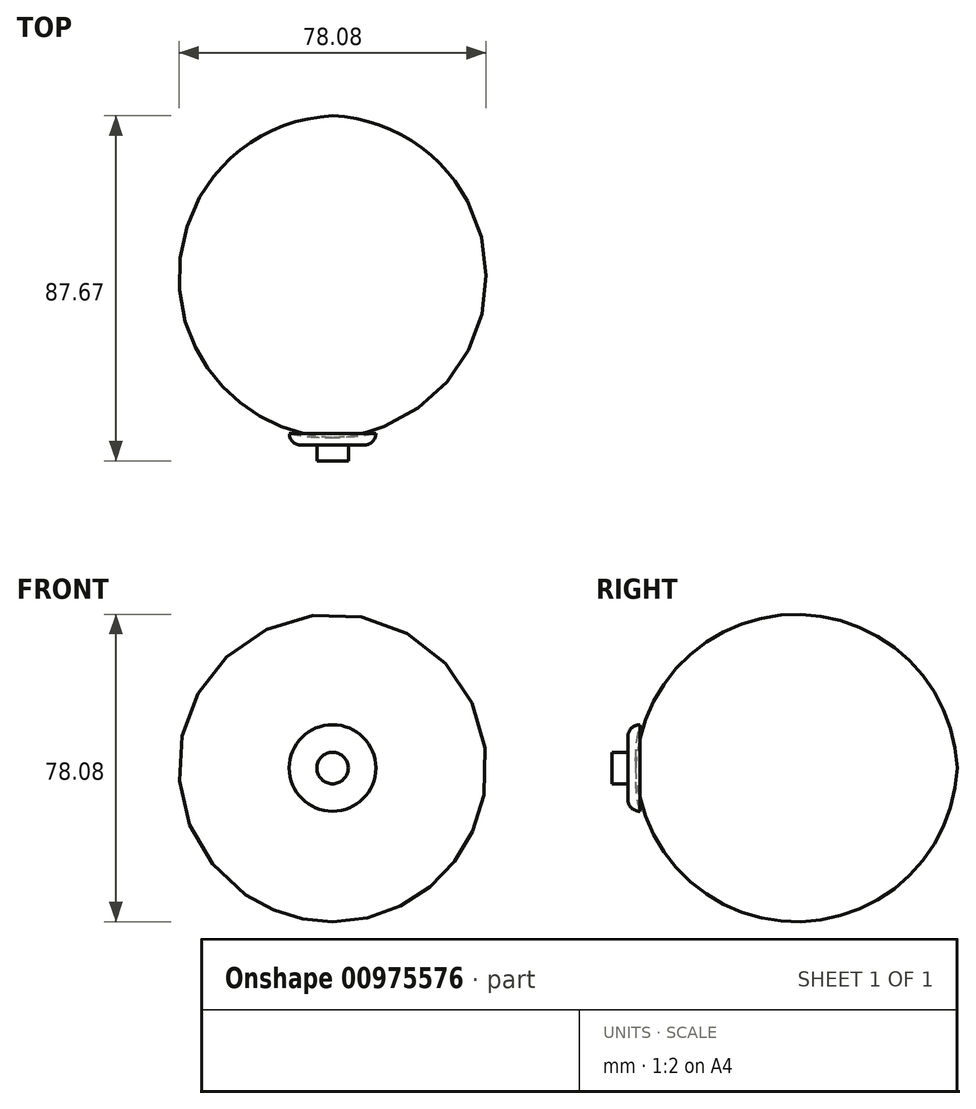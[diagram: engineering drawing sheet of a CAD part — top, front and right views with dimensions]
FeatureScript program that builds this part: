
annotation { "Feature Type Name" : "Feature", "Feature Type Description" : "" }
export const myFeature = defineFeature(function(context is Context, id is Id, definition is map)
    precondition{}
    {
        {
            var Q0;
            Q0=qCreatedBy(makeId("Top.planeOp"),FACE);
            var sketch = newSketch(context, id + "F0", { "sketchPlane" : qUnion([Q0])});
            skLineSegment(sketch, "E0", {"start": v(0, 0) * mm, "end": v(0, -2) * mm});
            skLineSegment(sketch, "E1", {"start": v(0, -2) * mm, "end": v(11, -2) * mm});
            skLineSegment(sketch, "E2", {"start": v(11, -2) * mm, "end": v(11, 1) * mm});
            skArc(sketch, "E3", {"start": v(0, 0) * mm, "mid": v(5.53, 0.13) * mm, "end": v(11, 1) * mm});
            skSolve(sketch);
        }
        {
            var Q0;
            Q0=makeQuery(id+"F0.imprint","IMPRINT",FACE,{"disambiguationData":[TD([[makeQuery(id+"F0.imprint","IMPRINT",EDGE,{"derivedFrom":sQuery(id+"F0.wireOp",EDGE,"E0")}),1.0]])]});
            var Q1;
            Q1=sQuery(id+"F0.wireOp",EDGE,"E0");
            revolve(context, id + "F1", {"surfaceOperationType" : NewSurfaceOperationType.NEW, "entities" : qUnion([Q0]), "axis" : qUnion([Q1]), "revolveType" : RevolveType.FULL});
        }
        {
            var Q0;
            Q0=makeQuery(id+"F1.opRevolve","SWEPT_FACE",FACE,{"disambiguationData":[OSD([sQuery(id+"F0.wireOp",EDGE,"E1")])]});
            var sketch = newSketch(context, id + "F2", { "sketchPlane" : qUnion([Q0])});
            skCircle(sketch, "E4", {"center": v(0, 0) * mm, "radius": 4 * mm});
            skSolve(sketch);
        }
        {
            var Q0;
            Q0 = qSketchRegion(id + "F2", true);
            extrude(context, id + "F3", {"entities" : qUnion([Q0]), "operationType" : NewBodyOperationType.ADD, "depth" : 4 * mm, "offsetDistance" : 25.4 * mm});
        }
        {
            var Q0;
            Q0=makeQuery(id+"F1.opRevolve","SWEPT_EDGE",EDGE,{"disambiguationData":[OSD([sQuery(id+"F0.wireOp",EDGE,"E1"),sQuery(id+"F0.wireOp",EDGE,"E2")])]});
            fillet(context, id + "F4", {"entities" : qUnion([Q0]), "radius" : 3 * mm, "tangentPropagation" : true, "allowEdgeOverflow" : false});
        }
    });
